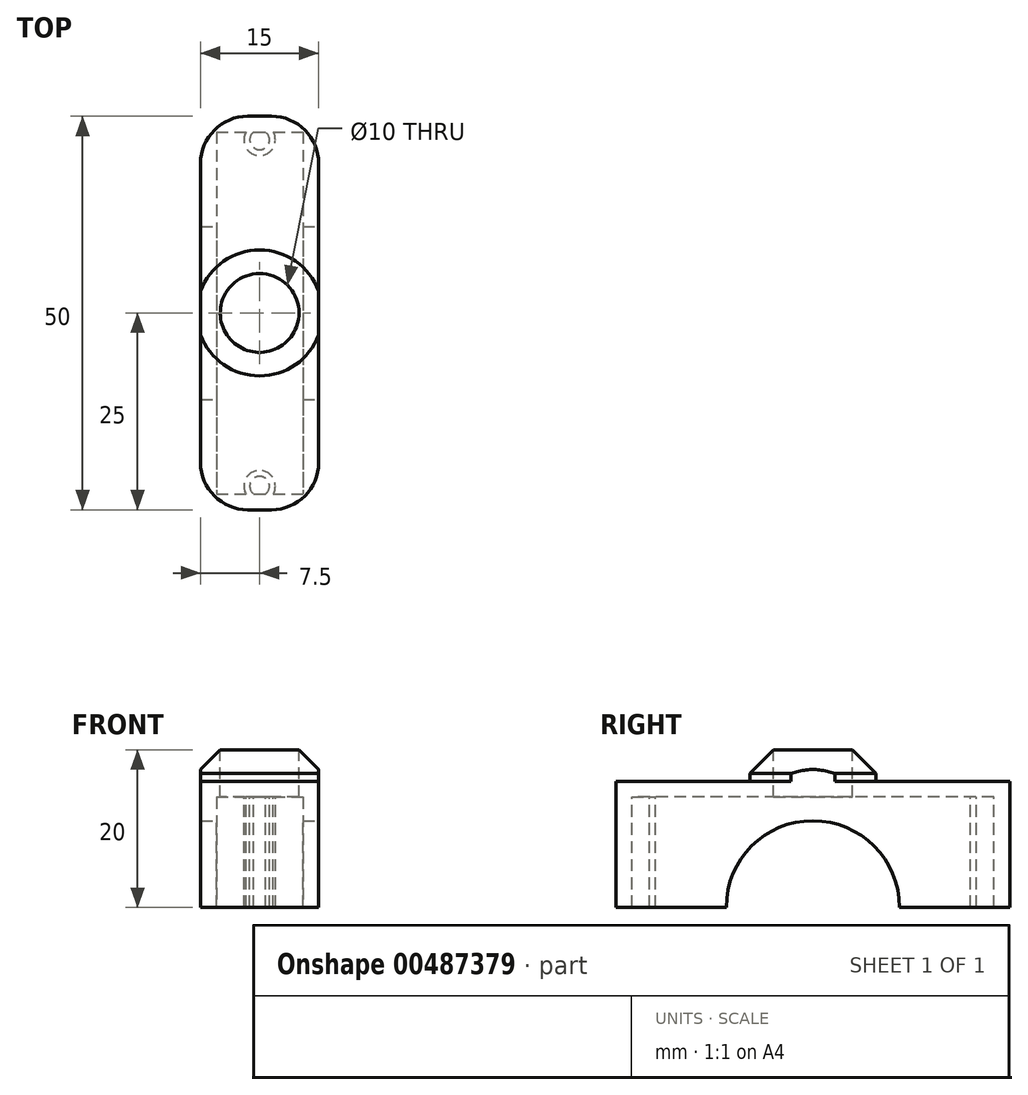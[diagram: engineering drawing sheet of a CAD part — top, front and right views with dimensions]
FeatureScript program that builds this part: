
annotation { "Feature Type Name" : "Feature", "Feature Type Description" : "" }
export const myFeature = defineFeature(function(context is Context, id is Id, definition is map)
    precondition{}
    {
        {
            var Q0;
            Q0=qCreatedBy(makeId("Top.planeOp"),FACE);
            var sketch = newSketch(context, id + "F0", { "sketchPlane" : qUnion([Q0])});
            skLineSegment(sketch, "E0.bottom", {"start": v(-15, 50) * mm, "end": v(0, 50) * mm});
            skLineSegment(sketch, "E0.top", {"start": v(-15, 0) * mm, "end": v(0, 0) * mm});
            skLineSegment(sketch, "E0.left", {"start": v(-15, 50) * mm, "end": v(-15, 0) * mm});
            skLineSegment(sketch, "E0.right", {"start": v(0, 50) * mm, "end": v(0, 0) * mm});
            skSolve(sketch);
        }
        {
            var Q0;
            Q0 = qSketchRegion(id + "F0", true);
            extrude(context, id + "F1", {"entities" : qUnion([Q0]), "depth" : 16 * mm});
        }
        {
            var Q0;
            Q0=makeQuery(id+"F1.opExtrude","SWEPT_FACE",FACE,{"disambiguationData":[OSD([sQuery(id+"F0.wireOp",EDGE,"E0.right")])]});
            var sketch = newSketch(context, id + "F2", { "sketchPlane" : qUnion([Q0])});
            skArc(sketch, "E1", {"start": v(36, 0) * mm, "mid": v(25, 11) * mm, "end": v(14, 0) * mm});
            skLineSegment(sketch, "E2", {"start": v(14, 0) * mm, "end": v(36, 0) * mm});
            skSolve(sketch);
        }
        {
            var Q0;
            Q0 = qSketchRegion(id + "F2", true);
            extrude(context, id + "F3", {"entities" : qUnion([Q0]), "operationType" : NewBodyOperationType.REMOVE, "oppositeDirection" : true, "depth" : 25 * mm});
        }
        {
            var Q0;
            Q0=makeQuery(id+"F3.boolean.opBoolean","COPY",FACE,{"derivedFrom":makeQuery(id+"F3.opExtrude","SWEPT_FACE",FACE,{"disambiguationData":[OSD([sQuery(id+"F2.wireOp",EDGE,"E1")])]})});
            var Q1;
            {var subQ0=sQuery(id+"F0.wireOp",EDGE,"E0.top");var subQ1=sQuery(id+"F0.wireOp",EDGE,"E0.left");var subQ2=sQuery(id+"F0.wireOp",EDGE,"E0.right");Q1=makeQuery(id+"F3.boolean.opBoolean","SPLIT",FACE,{"disambiguationData":[TD([makeQuery(id+"F1.opExtrude","SWEPT_FACE",FACE,{"disambiguationData":[OSD([subQ0])]})])],"derivedFrom":makeQuery(id+"F1.opExtrude","CAP_FACE",FACE,{"disambiguationData":[OSD([sQuery(id+"F0.wireOp",EDGE,"E0.bottom"),subQ0,subQ1,subQ2])],"isStart":true})});}
            var Q2;
            {var subQ0=sQuery(id+"F0.wireOp",EDGE,"E0.bottom");var subQ1=sQuery(id+"F0.wireOp",EDGE,"E0.right");var subQ2=sQuery(id+"F0.wireOp",EDGE,"E0.left");Q2=makeQuery(id+"F3.boolean.opBoolean","SPLIT",FACE,{"disambiguationData":[TD([makeQuery(id+"F1.opExtrude","SWEPT_FACE",FACE,{"disambiguationData":[OSD([subQ0])]})])],"derivedFrom":makeQuery(id+"F1.opExtrude","CAP_FACE",FACE,{"disambiguationData":[OSD([subQ0,sQuery(id+"F0.wireOp",EDGE,"E0.top"),subQ2,subQ1])],"isStart":true})});}
            shell(context, id + "F4", {"entities" : qUnion([Q0, Q1, Q2]), "thickness" : 2 * mm});
        }
        {
            var Q0;
            Q0=makeQuery(id+"F1.opExtrude","SWEPT_EDGE",EDGE,{"disambiguationData":[OSD([sQuery(id+"F0.wireOp",EDGE,"E0.top"),sQuery(id+"F0.wireOp",EDGE,"E0.right")])]});
            var Q1;
            Q1=makeQuery(id+"F1.opExtrude","SWEPT_EDGE",EDGE,{"disambiguationData":[OSD([sQuery(id+"F0.wireOp",EDGE,"E0.bottom"),sQuery(id+"F0.wireOp",EDGE,"E0.right")])]});
            var Q2;
            Q2=makeQuery(id+"F1.opExtrude","SWEPT_EDGE",EDGE,{"disambiguationData":[OSD([sQuery(id+"F0.wireOp",EDGE,"E0.bottom"),sQuery(id+"F0.wireOp",EDGE,"E0.left")])]});
            var Q3;
            Q3=makeQuery(id+"F1.opExtrude","SWEPT_EDGE",EDGE,{"disambiguationData":[OSD([sQuery(id+"F0.wireOp",EDGE,"E0.top"),sQuery(id+"F0.wireOp",EDGE,"E0.left")])]});
            fillet(context, id + "F5", {"entities" : qUnion([Q0, Q1, Q2, Q3]), "radius" : 6 * mm, "tangentPropagation" : true, "allowEdgeOverflow" : false});
        }
        {
            var Q0;
            Q0=makeQuery(id+"F1.opExtrude","CAP_FACE",FACE,{"disambiguationData":[OSD([sQuery(id+"F0.wireOp",EDGE,"E0.bottom"),sQuery(id+"F0.wireOp",EDGE,"E0.top"),sQuery(id+"F0.wireOp",EDGE,"E0.left"),sQuery(id+"F0.wireOp",EDGE,"E0.right")])],"isStart":false});
            var sketch = newSketch(context, id + "F6", { "sketchPlane" : qUnion([Q0])});
            skCircle(sketch, "E3", {"center": v(-7.5, 25) * mm, "radius": 5 * mm});
            skPoint(sketch, "E3.centerSnap0", {"position": v(-15, 25) * mm});
            skSolve(sketch);
        }
        {
            var Q0;
            Q0 = qSketchRegion(id + "F6", true);
            extrude(context, id + "F7", {"entities" : qUnion([Q0]), "operationType" : NewBodyOperationType.REMOVE, "oppositeDirection" : true, "depth" : 25 * mm});
        }
        {
            var Q0;
            Q0=makeQuery(id+"F1.opExtrude","CAP_FACE",FACE,{"disambiguationData":[OSD([sQuery(id+"F0.wireOp",EDGE,"E0.bottom"),sQuery(id+"F0.wireOp",EDGE,"E0.top"),sQuery(id+"F0.wireOp",EDGE,"E0.left"),sQuery(id+"F0.wireOp",EDGE,"E0.right")])],"isStart":false});
            var sketch = newSketch(context, id + "F8", { "sketchPlane" : qUnion([Q0])});
            skLineSegment(sketch, "E4", {"start": v(-15, 27.78) * mm, "end": v(-15, 22.22) * mm});
            skLineSegment(sketch, "E5", {"start": v(0, 27.78) * mm, "end": v(0, 22.22) * mm});
            skArc(sketch, "E6", {"start": v(0, 27.78) * mm, "mid": v(-7.5, 33) * mm, "end": v(-15, 27.78) * mm});
            skArc(sketch, "E7", {"start": v(-15, 22.22) * mm, "mid": v(-7.5, 17) * mm, "end": v(0, 22.22) * mm});
            skSolve(sketch);
        }
        {
            var Q0;
            Q0 = qSketchRegion(id + "F8", true);
            extrude(context, id + "F9", {"entities" : qUnion([Q0]), "operationType" : NewBodyOperationType.ADD, "depth" : 4 * mm});
        }
        {
            var Q0;
            Q0=makeQuery(id+"F9.opExtrude","CAP_FACE",FACE,{"disambiguationData":[OSD([sQuery(id+"F8.wireOp",EDGE,"E4"),sQuery(id+"F8.wireOp",EDGE,"E5"),sQuery(id+"F8.wireOp",EDGE,"E6"),sQuery(id+"F8.wireOp",EDGE,"E7")])],"isStart":false});
            var sketch = newSketch(context, id + "F10", { "sketchPlane" : qUnion([Q0])});
            skCircle(sketch, "E8", {"center": v(-7.5, 25) * mm, "radius": 5 * mm});
            skSolve(sketch);
        }
        {
            var Q0;
            Q0 = qSketchRegion(id + "F10", true);
            extrude(context, id + "F11", {"entities" : qUnion([Q0]), "operationType" : NewBodyOperationType.REMOVE, "oppositeDirection" : true, "depth" : 25 * mm});
        }
        {
            var Q0;
            Q0=makeQuery(id+"F9.opExtrude","CAP_EDGE",EDGE,{"disambiguationData":[OSD([sQuery(id+"F8.wireOp",EDGE,"E7")])],"isStart":false});
            var Q1;
            Q1=makeQuery(id+"F9.opExtrude","CAP_EDGE",EDGE,{"disambiguationData":[OSD([sQuery(id+"F8.wireOp",EDGE,"E5")])],"isStart":false});
            var Q2;
            Q2=makeQuery(id+"F9.opExtrude","CAP_EDGE",EDGE,{"disambiguationData":[OSD([sQuery(id+"F8.wireOp",EDGE,"E6")])],"isStart":false});
            var Q3;
            Q3=makeQuery(id+"F9.opExtrude","CAP_EDGE",EDGE,{"disambiguationData":[OSD([sQuery(id+"F8.wireOp",EDGE,"E4")])],"isStart":false});
            chamfer(context, id + "F12", {"entities" : qUnion([Q0, Q1, Q2, Q3]), "width" : 3 * mm, "tangentPropagation" : true});
        }
        {
            var Q0;
            Q0=makeQuery(id+"F4.opShell","OFFSET_FACE",FACE,{"disambiguationData":[OSD([sQuery(id+"F0.wireOp",EDGE,"E0.bottom"),sQuery(id+"F0.wireOp",EDGE,"E0.top"),sQuery(id+"F0.wireOp",EDGE,"E0.left"),sQuery(id+"F0.wireOp",EDGE,"E0.right")])]});
            var sketch = newSketch(context, id + "F13", { "sketchPlane" : qUnion([Q0])});
            skCircle(sketch, "E9", {"center": v(-7.5, -3) * mm, "radius": 2 * mm});
            skCircle(sketch, "E10", {"center": v(-7.5, -3) * mm, "radius": 1.25 * mm});
            skLineSegment(sketch, "E11", {"start": v(-13, -25) * mm, "end": v(-2, -25) * mm, "construction": true});
            skCircle(sketch, "E12.MirrorC", {"center": v(-7.5, -47) * mm, "radius": 2 * mm});
            skCircle(sketch, "E13.MirrorC", {"center": v(-7.5, -47) * mm, "radius": 1.25 * mm});
            skSolve(sketch);
        }
        {
            var Q0;
            Q0 = qSketchRegion(id + "F13", true);
            extrude(context, id + "F14", {"entities" : qUnion([Q0]), "operationType" : NewBodyOperationType.ADD, "depth" : 14 * mm});
        }
    });
